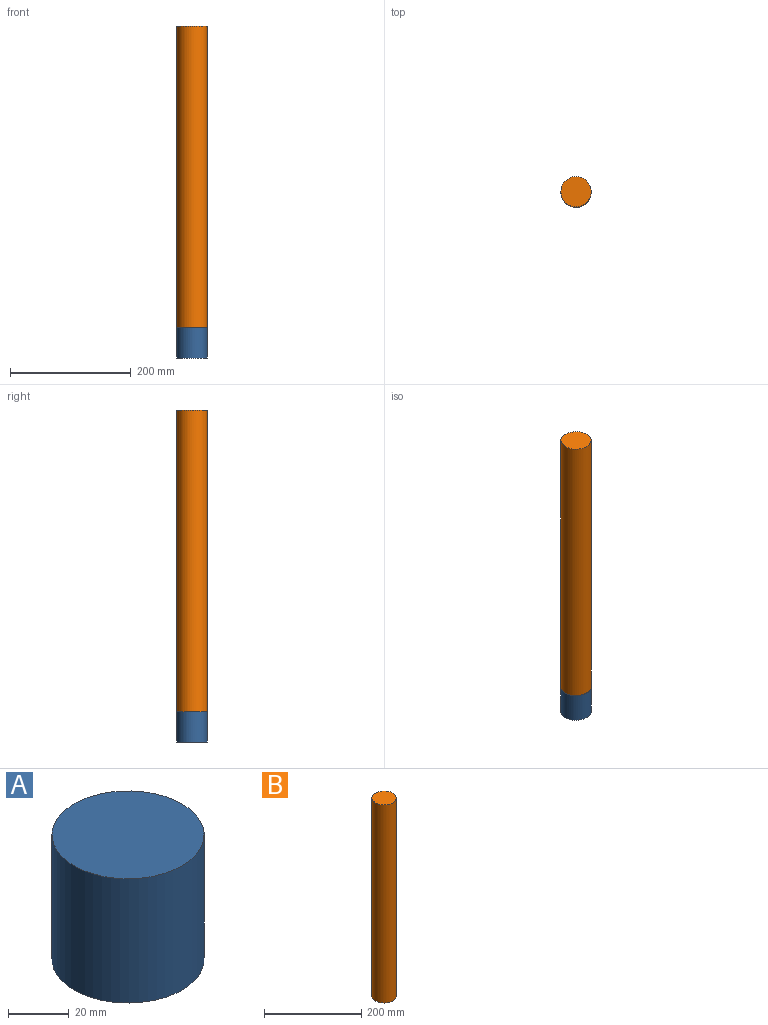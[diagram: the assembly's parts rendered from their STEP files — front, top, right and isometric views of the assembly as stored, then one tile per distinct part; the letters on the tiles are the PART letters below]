
ASSEMBLY  parts=2 mates=1
PART A: 3 faces, bbox 50x50x50 mm
  f0: cylinder r=25mm len=50mm, axis (0,0,1), area 7854mm2, adj f1,f2
  f1: plane 50x50mm, normal (0,0,-1), area 1963.5mm2, adj f0
  f2: plane 50x50mm, normal (0,0,1), area 1963.5mm2, adj f0
PART B: 3 faces, bbox 50x50x500 mm
  f0: cylinder r=25mm len=500mm, axis (0,0,1), area 78539.8mm2, adj f1,f2
  f1: plane 50x50mm, normal (0,0,-1), area 1963.5mm2, adj f0
  f2: plane 50x50mm, normal (0,0,1), area 1963.5mm2, adj f0
PLACE A t=(0,0,-500)mm
PLACE B rot(axis=(0,0,1),180deg) t=(0,0,0)mm
MATE planar B.f0 <-> A.f0  axis (0,0,1) through (0,0,0)mm
